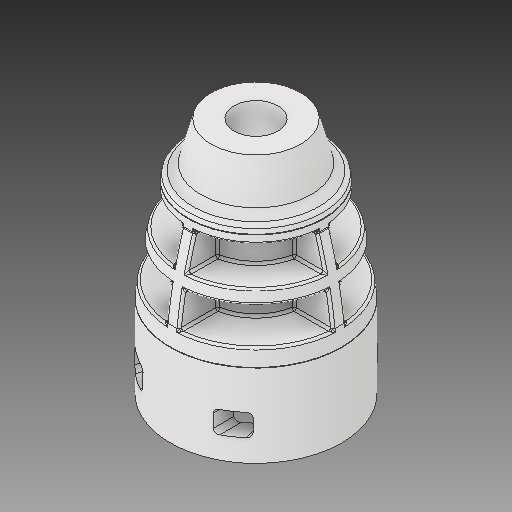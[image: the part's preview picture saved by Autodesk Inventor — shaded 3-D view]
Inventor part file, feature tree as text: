
AUTODESK INVENTOR PART (.ipt)
format: ipt  version: 2018 (Build 220112000, 112)  size: 834,048 bytes
history: native  units: in
note: dims shown in document units (in); Inventor stores cm internally (conversion verified against a paired STEP export)
features: fillet x1
ambient origin geometry x8: Origin, YZ Plane, XZ Plane, XY Plane, X Axis, Y Axis, Z Axis, Center Point
bodies: Solid1 (feature_tree)
feature tree (1):
  fillet  "Fillet3"  [1 undecoded]
note: 1 required parameter value undecoded (feature->parameter linkage not recoverable at this tier; creation-order binding heuristic only, values carry confidence <= 0.55)
